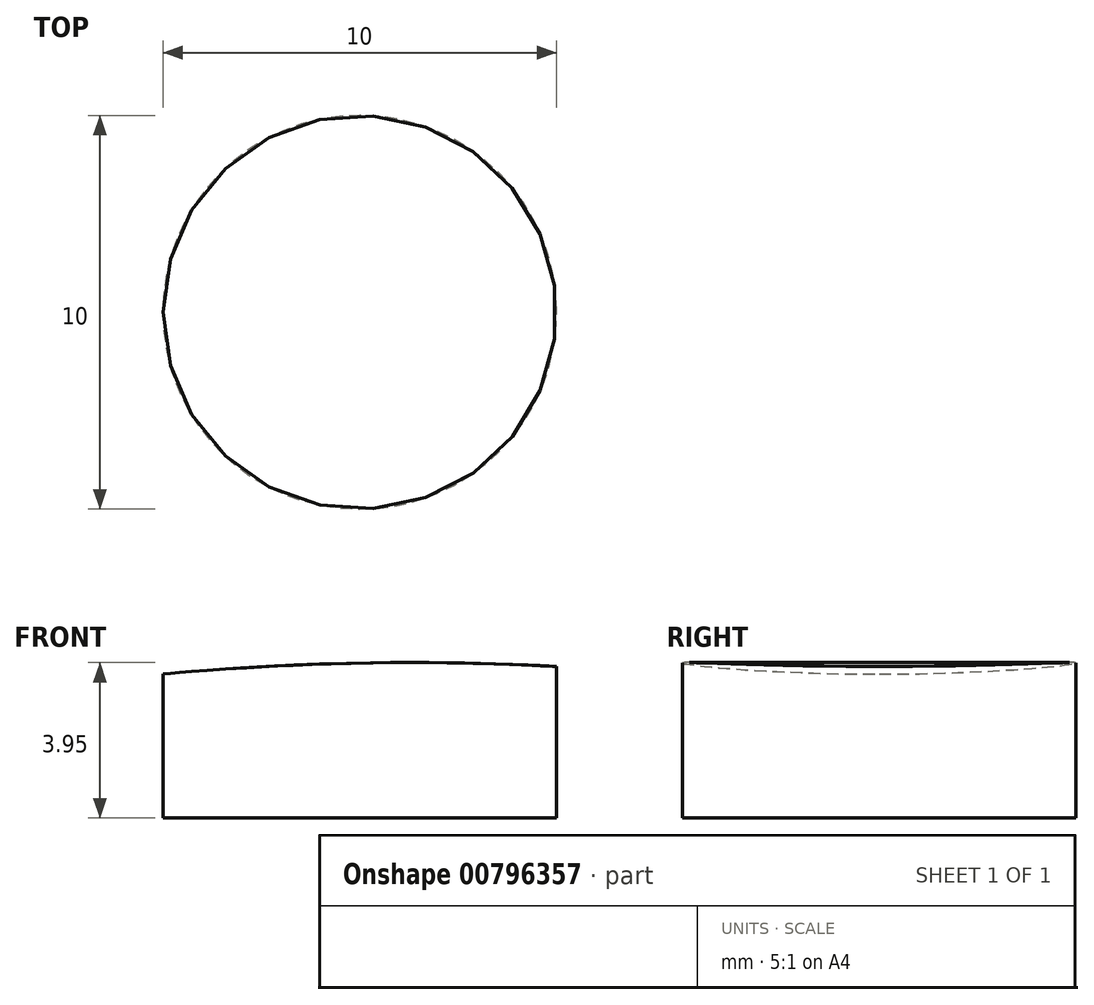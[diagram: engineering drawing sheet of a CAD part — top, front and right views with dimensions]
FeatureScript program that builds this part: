
annotation { "Feature Type Name" : "Feature", "Feature Type Description" : "" }
export const myFeature = defineFeature(function(context is Context, id is Id, definition is map)
    precondition{}
    {
        {
            var Q0;
            Q0=qCreatedBy(makeId("Top.planeOp"),FACE);
            var sketch = newSketch(context, id + "F0", { "sketchPlane" : qUnion([Q0])});
            skCircle(sketch, "E0", {"center": v(0, 0) * mm, "radius": 5 * mm});
            skSolve(sketch);
        }
        {
            var Q0;
            Q0 = qSketchRegion(id + "F0", true);
            extrude(context, id + "F1", {"entities" : qUnion([Q0]), "depth" : 4 * mm, "offsetDistance" : 25 * mm});
        }
        {
            var Q0;
            Q0=qCreatedBy(makeId("Front.planeOp"),FACE);
            var sketch = newSketch(context, id + "F2", { "sketchPlane" : qUnion([Q0])});
            skArc(sketch, "E1", {"start": v(35.18, -5.26) * mm, "mid": v(0.59, 3.95) * mm, "end": v(-33.81, -5.98) * mm});
            skLineSegment(sketch, "E2", {"start": v(35.18, -5.26) * mm, "end": v(35.18, 7.93) * mm});
            skLineSegment(sketch, "E3", {"start": v(35.18, 7.93) * mm, "end": v(-33.81, 7.93) * mm});
            skLineSegment(sketch, "E4", {"start": v(-33.81, 7.93) * mm, "end": v(-33.81, -5.98) * mm});
            skSolve(sketch);
        }
        {
            var Q0;
            Q0 = qSketchRegion(id + "F2", true);
            extrude(context, id + "F3", {"entities" : qUnion([Q0]), "operationType" : NewBodyOperationType.REMOVE, "depth" : 25 * mm, "offsetDistance" : 25 * mm, "hasSecondDirection" : true, "secondDirectionOppositeDirection" : true, "secondDirectionDepth" : 25 * mm});
        }
    });
